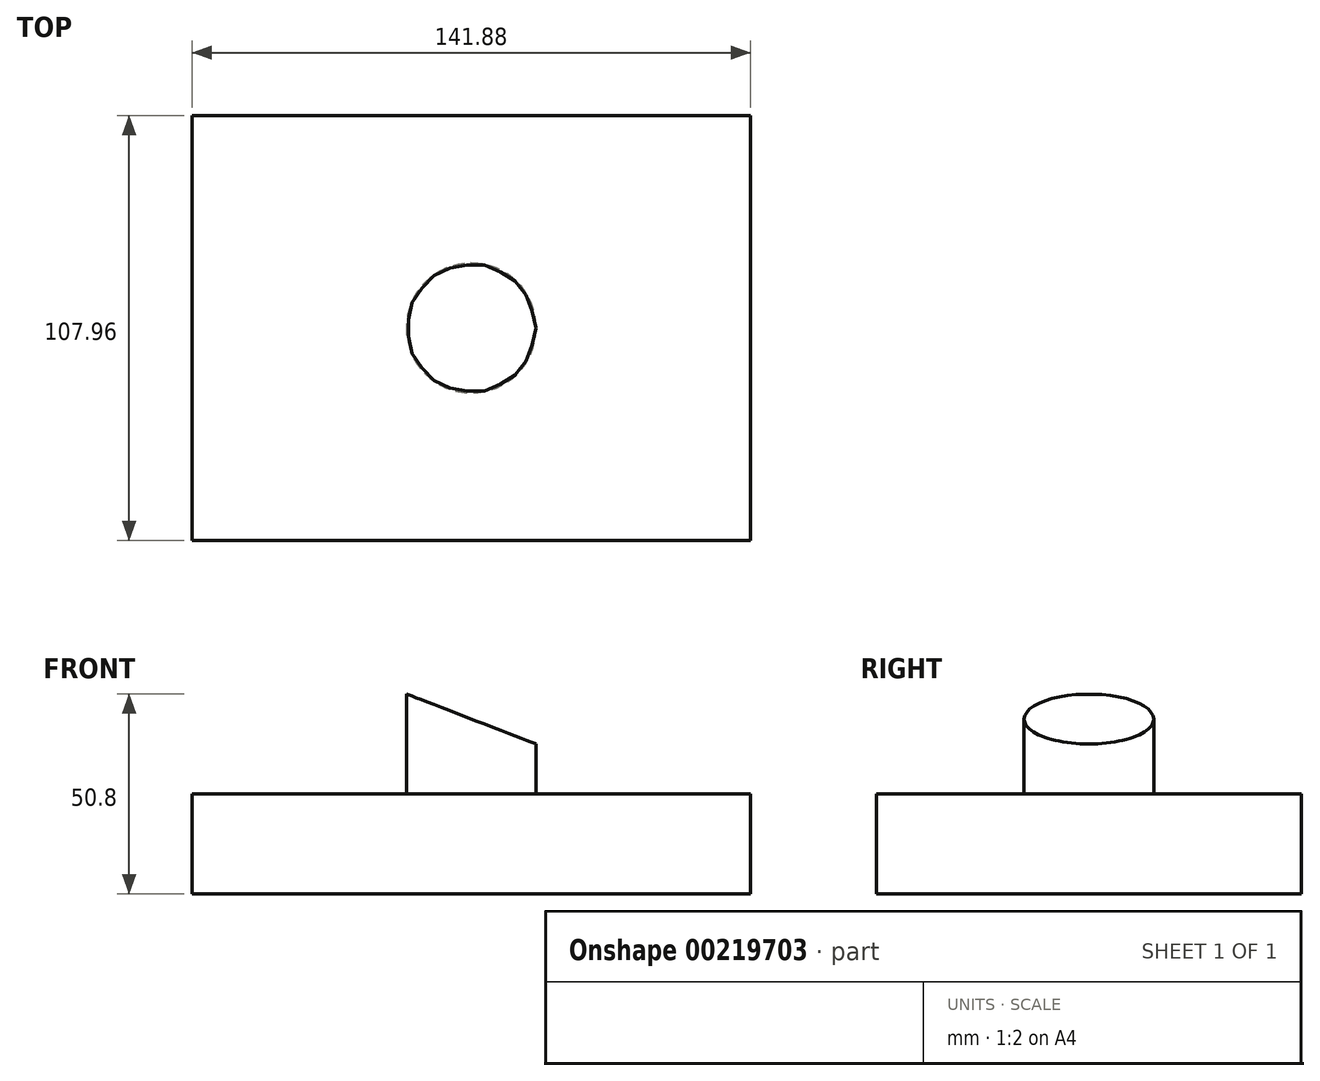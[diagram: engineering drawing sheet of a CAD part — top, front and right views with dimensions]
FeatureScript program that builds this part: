
annotation { "Feature Type Name" : "Feature", "Feature Type Description" : "" }
export const myFeature = defineFeature(function(context is Context, id is Id, definition is map)
    precondition{}
    {
        {
            var Q0;
            Q0=qCreatedBy(makeId("Top.planeOp"),FACE);
            var sketch = newSketch(context, id + "F0", { "sketchPlane" : qUnion([Q0])});
            skLineSegment(sketch, "E0.bottom", {"start": v(-70.94, 53.98) * mm, "end": v(70.94, 53.98) * mm});
            skLineSegment(sketch, "E0.top", {"start": v(-70.94, -53.98) * mm, "end": v(70.94, -53.98) * mm});
            skLineSegment(sketch, "E0.left", {"start": v(-70.94, 53.98) * mm, "end": v(-70.94, -53.98) * mm});
            skLineSegment(sketch, "E0.right", {"start": v(70.94, 53.98) * mm, "end": v(70.94, -53.98) * mm});
            skPoint(sketch, "E0.middle", {"position": v(0, 0) * mm});
            skCircle(sketch, "E1", {"center": v(0, 0) * mm, "radius": 16.48 * mm});
            skSolve(sketch);
        }
        {
            var Q0;
            Q0=makeQuery(id+"F0.imprint","IMPRINT",FACE,{"disambiguationData":[TD([[makeQuery(id+"F0.imprint","IMPRINT",EDGE,{"derivedFrom":sQuery(id+"F0.wireOp",EDGE,"E1")}),1.0]])]});
            extrude(context, id + "F1", {"entities" : qUnion([Q0]), "depth" : 50.8 * mm});
        }
        {
            var Q0;
            Q0 = qSketchRegion(id + "F0", true);
            extrude(context, id + "F2", {"entities" : qUnion([Q0]), "operationType" : NewBodyOperationType.ADD, "depth" : 25.4 * mm});
        }
        {
            var Q0;
            Q0=makeQuery(id+"F2.opExtrude","SWEPT_FACE",FACE,{"disambiguationData":[OSD([sQuery(id+"F0.wireOp",EDGE,"E0.top")])]});
            var sketch = newSketch(context, id + "F3", { "sketchPlane" : qUnion([Q0])});
            skLineSegment(sketch, "E2.0", {"start": v(-16.48, 50.8) * mm, "end": v(16.48, 50.8) * mm});
            skLineSegment(sketch, "E3", {"start": v(16.48, 50.8) * mm, "end": v(16.48, 25.4) * mm});
            skLineSegment(sketch, "E4", {"start": v(-16.48, 50.8) * mm, "end": v(16.48, 38.1) * mm});
            skSolve(sketch);
        }
        {
            var Q0;
            {var subQ0=sQuery(id+"F3.wireOp",EDGE,"E2.0");Q0=makeQuery(id+"F3.imprint","IMPRINT",FACE,{"disambiguationData":[TD([[makeQuery(id+"F3.imprint","IMPRINT",EDGE,{"derivedFrom":subQ0}),-1.0]])]});}
            extrude(context, id + "F4", {"entities" : qUnion([Q0]), "operationType" : NewBodyOperationType.REMOVE, "endBound" : BoundingType.THROUGH_ALL, "oppositeDirection" : true, "depth" : 25.4 * mm});
        }
    });
